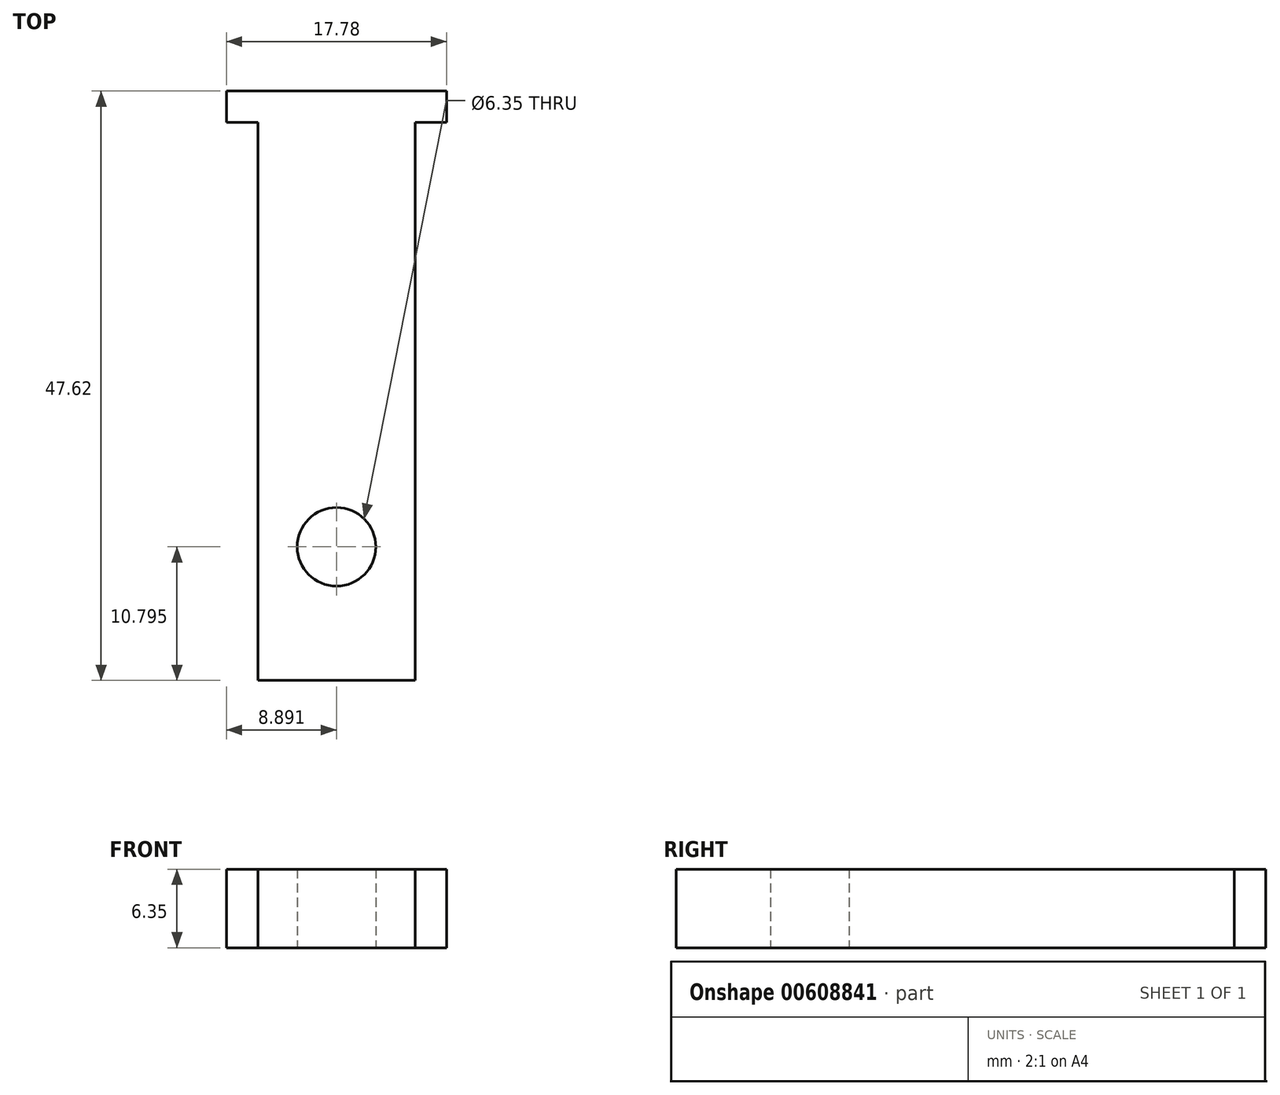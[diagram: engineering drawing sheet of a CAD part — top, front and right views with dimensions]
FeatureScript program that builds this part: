
annotation { "Feature Type Name" : "Feature", "Feature Type Description" : "" }
export const myFeature = defineFeature(function(context is Context, id is Id, definition is map)
    precondition{}
    {
        {
            var Q0;
            Q0=qCreatedBy(makeId("Top.planeOp"),FACE);
            var sketch = newSketch(context, id + "F0", { "sketchPlane" : qUnion([Q0])});
            skLineSegment(sketch, "E0.bottom", {"start": v(0, 0) * mm, "end": v(-6.35, 0) * mm});
            skLineSegment(sketch, "E0.left", {"start": v(0, 0) * mm, "end": v(0, 45.09) * mm});
            skLineSegment(sketch, "E0.right", {"start": v(-6.35, 0) * mm, "end": v(-6.35, 45.09) * mm});
            skLineSegment(sketch, "E1.bottom", {"start": v(-6.35, 45.09) * mm, "end": v(-8.89, 45.09) * mm});
            skLineSegment(sketch, "E1.top", {"start": v(0, 47.62) * mm, "end": v(-8.89, 47.62) * mm});
            skLineSegment(sketch, "E1.left", {"start": v(0, 45.09) * mm, "end": v(0, 47.62) * mm});
            skLineSegment(sketch, "E1.right", {"start": v(-8.89, 45.09) * mm, "end": v(-8.89, 47.62) * mm});
            skLineSegment(sketch, "E2", {"start": v(0, 47.62) * mm, "end": v(0, 10.8) * mm});
            skCircle(sketch, "E3", {"center": v(0, 10.8) * mm, "radius": 2.54 * mm});
            skLineSegment(sketch, "E4.bottom", {"start": v(34.47, -9.73) * mm, "end": v(28.12, -9.73) * mm});
            skLineSegment(sketch, "E4.left", {"start": v(34.47, -9.73) * mm, "end": v(34.47, -2.11) * mm});
            skLineSegment(sketch, "E4.right", {"start": v(28.12, -9.73) * mm, "end": v(28.12, 35.35) * mm});
            skLineSegment(sketch, "E5.bottom", {"start": v(28.12, 35.35) * mm, "end": v(25.58, 35.35) * mm});
            skLineSegment(sketch, "E5.top", {"start": v(34.47, 37.9) * mm, "end": v(25.58, 37.9) * mm});
            skLineSegment(sketch, "E5.left", {"start": v(34.47, 35.35) * mm, "end": v(34.47, 37.9) * mm});
            skLineSegment(sketch, "E5.right", {"start": v(25.58, 35.35) * mm, "end": v(25.58, 37.9) * mm});
            skLineSegment(sketch, "E6", {"start": v(34.47, 37.9) * mm, "end": v(34.47, 1.06) * mm});
            skLineSegment(sketch, "E7.MirrorCS", {"start": v(40.82, 35.35) * mm, "end": v(43.36, 35.35) * mm});
            skLineSegment(sketch, "E8.MirrorCS", {"start": v(43.36, 35.35) * mm, "end": v(43.36, 37.9) * mm});
            skLineSegment(sketch, "E9.MirrorCS", {"start": v(40.82, -9.73) * mm, "end": v(40.82, 35.35) * mm});
            skLineSegment(sketch, "E10.MirrorCS", {"start": v(34.47, -9.73) * mm, "end": v(40.82, -9.73) * mm});
            skLineSegment(sketch, "E11.MirrorCS", {"start": v(34.47, 37.9) * mm, "end": v(43.36, 37.9) * mm});
            skCircle(sketch, "E12", {"center": v(34.47, 1.06) * mm, "radius": 3.18 * mm});
            skLineSegment(sketch, "E13.trimOffspring", {"start": v(34.47, 4.24) * mm, "end": v(34.47, 35.35) * mm});
            skSolve(sketch);
        }
        {
            var Q0;
            {var subQ0=sQuery(id+"F0.wireOp",EDGE,"E4.left");Q0=makeQuery(id+"F0.imprint","IMPRINT",FACE,{"disambiguationData":[TD([[makeQuery(id+"F0.imprint","IMPRINT",EDGE,{"derivedFrom":subQ0}),-1.0]])]});}
            var Q1;
            Q1=makeQuery(id+"F0.imprint","IMPRINT",FACE,{"disambiguationData":[TD([[makeQuery(id+"F0.imprint","IMPRINT",EDGE,{"derivedFrom":sQuery(id+"F0.wireOp",EDGE,"E4.bottom")}),-1.0]])]});
            extrude(context, id + "F1", {"entities" : qUnion([Q0, Q1]), "depth" : 6.35 * mm, "offsetDistance" : 25.4 * mm});
        }
    });
